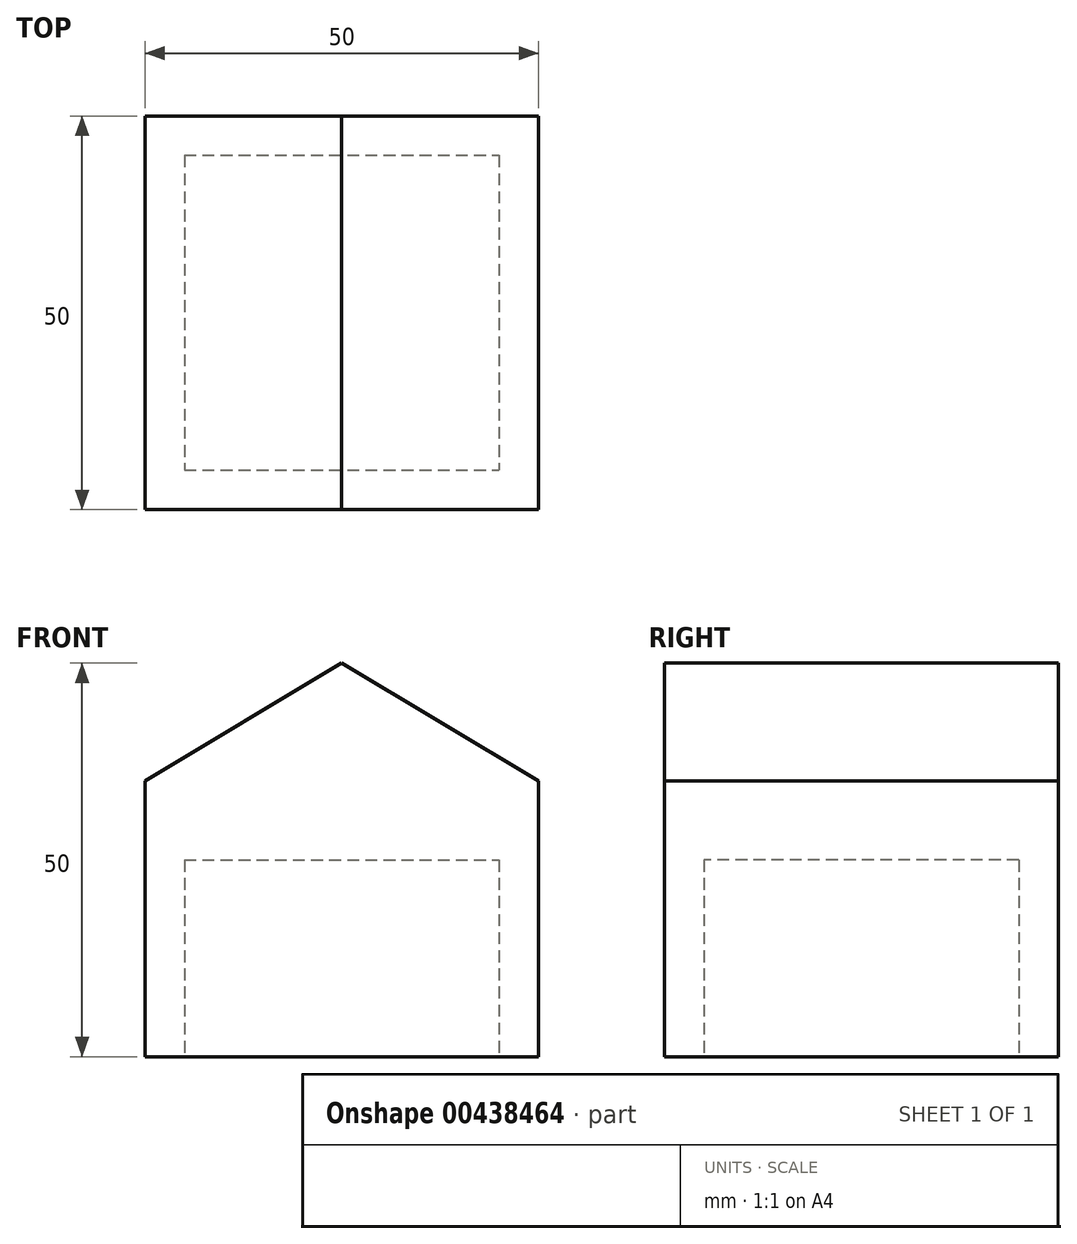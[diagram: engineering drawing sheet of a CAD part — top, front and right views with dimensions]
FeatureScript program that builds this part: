
annotation { "Feature Type Name" : "Feature", "Feature Type Description" : "" }
export const myFeature = defineFeature(function(context is Context, id is Id, definition is map)
    precondition{}
    {
        {
            var Q0;
            Q0=qCreatedBy(makeId("Top.planeOp"),FACE);
            var sketch = newSketch(context, id + "F0", { "sketchPlane" : qUnion([Q0])});
            skLineSegment(sketch, "E0.bottom", {"start": v(-9.63, 2.1) * mm, "end": v(-59.63, 2.1) * mm});
            skLineSegment(sketch, "E0.top", {"start": v(-9.63, 52.1) * mm, "end": v(-59.63, 52.1) * mm});
            skLineSegment(sketch, "E0.left", {"start": v(-9.63, 2.1) * mm, "end": v(-9.63, 52.1) * mm});
            skLineSegment(sketch, "E0.right", {"start": v(-59.63, 2.1) * mm, "end": v(-59.63, 52.1) * mm});
            skLineSegment(sketch, "E1.bottom", {"start": v(-54.63, 47.1) * mm, "end": v(-14.63, 47.1) * mm});
            skLineSegment(sketch, "E1.top", {"start": v(-54.63, 7.1) * mm, "end": v(-14.63, 7.1) * mm});
            skLineSegment(sketch, "E1.left", {"start": v(-54.63, 47.1) * mm, "end": v(-54.63, 7.1) * mm});
            skLineSegment(sketch, "E1.right", {"start": v(-14.63, 47.1) * mm, "end": v(-14.63, 7.1) * mm});
            skSolve(sketch);
        }
        {
            var Q0;
            Q0=makeQuery(id+"F0.imprint","IMPRINT",FACE,{"disambiguationData":[TD([[makeQuery(id+"F0.imprint","IMPRINT",EDGE,{"derivedFrom":sQuery(id+"F0.wireOp",EDGE,"E0.bottom")}),-1.0]])]});
            extrude(context, id + "F1", {"entities" : qUnion([Q0]), "depth" : 25 * mm});
        }
        {
            var Q0;
            Q0=makeQuery(id+"F1.opExtrude","CAP_FACE",FACE,{"disambiguationData":[OSD([sQuery(id+"F0.wireOp",EDGE,"E0.bottom"),sQuery(id+"F0.wireOp",EDGE,"E0.top"),sQuery(id+"F0.wireOp",EDGE,"E0.left"),sQuery(id+"F0.wireOp",EDGE,"E0.right"),sQuery(id+"F0.wireOp",EDGE,"E1.bottom"),sQuery(id+"F0.wireOp",EDGE,"E1.top"),sQuery(id+"F0.wireOp",EDGE,"E1.left"),sQuery(id+"F0.wireOp",EDGE,"E1.right")])],"isStart":false});
            var sketch = newSketch(context, id + "F2", { "sketchPlane" : qUnion([Q0])});
            skLineSegment(sketch, "E2.bottom", {"start": v(-59.63, 52.1) * mm, "end": v(-9.63, 52.1) * mm});
            skLineSegment(sketch, "E2.top", {"start": v(-59.63, 2.1) * mm, "end": v(-9.63, 2.1) * mm});
            skLineSegment(sketch, "E2.left", {"start": v(-59.63, 52.1) * mm, "end": v(-59.63, 2.1) * mm});
            skLineSegment(sketch, "E2.right", {"start": v(-9.63, 52.1) * mm, "end": v(-9.63, 2.1) * mm});
            skSolve(sketch);
        }
        {
            var Q0;
            Q0 = qSketchRegion(id + "F2", true);
            extrude(context, id + "F3", {"entities" : qUnion([Q0]), "operationType" : NewBodyOperationType.ADD, "depth" : 25 * mm});
        }
        {
            var Q0;
            Q0=makeQuery(id+"F3.opExtrude","CAP_EDGE",EDGE,{"disambiguationData":[OSD([sQuery(id+"F2.wireOp",EDGE,"E2.left")])],"isStart":false});
            var Q1;
            Q1=makeQuery(id+"F3.opExtrude","CAP_EDGE",EDGE,{"disambiguationData":[OSD([sQuery(id+"F2.wireOp",EDGE,"E2.right")])],"isStart":false});
            chamfer(context, id + "F4", {"entities" : qUnion([Q0, Q1]), "chamferType" : ChamferType.TWO_OFFSETS, "width1" : 15 * mm, "oppositeDirection" : false, "width2" : 25 * mm, "tangentPropagation" : true});
        }
    });
